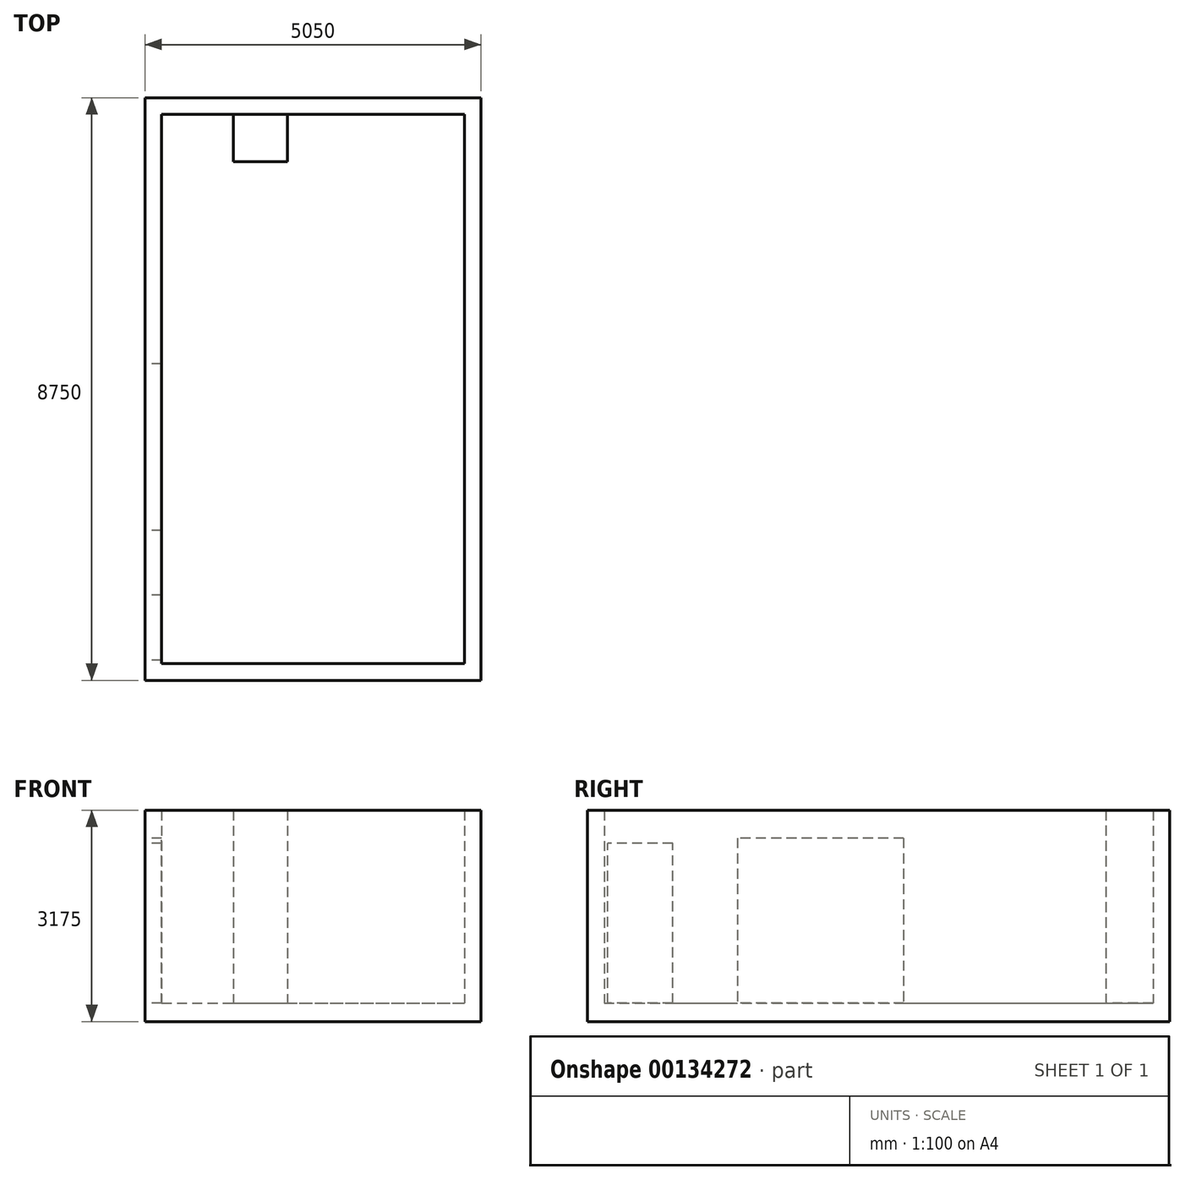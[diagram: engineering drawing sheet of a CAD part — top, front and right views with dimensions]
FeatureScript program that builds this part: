
annotation { "Feature Type Name" : "Feature", "Feature Type Description" : "" }
export const myFeature = defineFeature(function(context is Context, id is Id, definition is map)
    precondition{}
    {
        {
            var Q0;
            Q0=qCreatedBy(makeId("Top.planeOp"),FACE);
            var sketch = newSketch(context, id + "F0", { "sketchPlane" : qUnion([Q0])});
            skLineSegment(sketch, "E0.bottom", {"start": v(0, 0) * mm, "end": v(4550, 0) * mm});
            skLineSegment(sketch, "E0.top", {"start": v(0, 8250) * mm, "end": v(4550, 8250) * mm});
            skLineSegment(sketch, "E0.left", {"start": v(0, 0) * mm, "end": v(0, 8250) * mm});
            skLineSegment(sketch, "E0.right", {"start": v(4550, 0) * mm, "end": v(4550, 8250) * mm});
            skSolve(sketch);
        }
        {
            var Q0;
            Q0 = qSketchRegion(id + "F0", true);
            extrude(context, id + "F1", {"entities" : qUnion([Q0]), "depth" : 2920 * mm});
        }
        {
            var Q0;
            Q0=makeQuery(id+"F1.opExtrude","CAP_FACE",FACE,{"disambiguationData":[OSD([sQuery(id+"F0.wireOp",EDGE,"E0.bottom"),sQuery(id+"F0.wireOp",EDGE,"E0.top"),sQuery(id+"F0.wireOp",EDGE,"E0.left"),sQuery(id+"F0.wireOp",EDGE,"E0.right")])],"isStart":false});
            shell(context, id + "F2", {"entities" : qUnion([Q0]), "thickness" : 250 * mm, "oppositeDirection" : true});
        }
        {
            var Q0;
            Q0=makeQuery(id+"F2.opShell","OFFSET_FACE",FACE,{"disambiguationData":[OSD([sQuery(id+"F0.wireOp",EDGE,"E0.bottom"),sQuery(id+"F0.wireOp",EDGE,"E0.top"),sQuery(id+"F0.wireOp",EDGE,"E0.left"),sQuery(id+"F0.wireOp",EDGE,"E0.right")])]});
            extrude(context, id + "F3", {"entities" : qUnion([Q0]), "operationType" : NewBodyOperationType.ADD, "depth" : 25 * mm});
        }
        {
            var Q0;
            Q0=makeQuery(id+"F3.opExtrude","CAP_FACE",FACE,{"disambiguationData":[OSD([sQuery(id+"F0.wireOp",EDGE,"E0.bottom"),sQuery(id+"F0.wireOp",EDGE,"E0.top"),sQuery(id+"F0.wireOp",EDGE,"E0.left"),sQuery(id+"F0.wireOp",EDGE,"E0.right")])],"isStart":false});
            var sketch = newSketch(context, id + "F4", { "sketchPlane" : qUnion([Q0])});
            skLineSegment(sketch, "E1.bottom", {"start": v(1077, 8250) * mm, "end": v(1887, 8250) * mm});
            skLineSegment(sketch, "E1.top", {"start": v(1077, 7540) * mm, "end": v(1887, 7540) * mm});
            skLineSegment(sketch, "E1.left", {"start": v(1077, 8250) * mm, "end": v(1077, 7540) * mm});
            skLineSegment(sketch, "E1.right", {"start": v(1887, 8250) * mm, "end": v(1887, 7540) * mm});
            skSolve(sketch);
        }
        {
            var Q0;
            Q0 = qSketchRegion(id + "F4", true);
            extrude(context, id + "F5", {"entities" : qUnion([Q0]), "operationType" : NewBodyOperationType.ADD, "depth" : 2900 * mm});
        }
        {
            var Q0;
            Q0=makeQuery(id+"F1.opExtrude","SWEPT_FACE",FACE,{"disambiguationData":[OSD([sQuery(id+"F0.wireOp",EDGE,"E0.left")])]});
            var sketch = newSketch(context, id + "F6", { "sketchPlane" : qUnion([Q0])});
            skLineSegment(sketch, "E2.bottom", {"start": v(-1030, 25) * mm, "end": v(-50, 25) * mm});
            skLineSegment(sketch, "E2.top", {"start": v(-1030, 2425) * mm, "end": v(-50, 2425) * mm});
            skLineSegment(sketch, "E2.left", {"start": v(-1030, 25) * mm, "end": v(-1030, 2425) * mm});
            skLineSegment(sketch, "E2.right", {"start": v(-50, 25) * mm, "end": v(-50, 2425) * mm});
            skSolve(sketch);
        }
        {
            var Q0;
            Q0 = qSketchRegion(id + "F6", true);
            extrude(context, id + "F7", {"entities" : qUnion([Q0]), "operationType" : NewBodyOperationType.REMOVE, "oppositeDirection" : true, "depth" : 300 * mm});
        }
        {
            var Q0;
            Q0=makeQuery(id+"F1.opExtrude","SWEPT_FACE",FACE,{"disambiguationData":[OSD([sQuery(id+"F0.wireOp",EDGE,"E0.left")])]});
            var sketch = newSketch(context, id + "F8", { "sketchPlane" : qUnion([Q0])});
            skLineSegment(sketch, "E3.bottom", {"start": v(-4500, 2505) * mm, "end": v(-2000, 2505) * mm});
            skLineSegment(sketch, "E3.top", {"start": v(-4500, 25) * mm, "end": v(-2000, 25) * mm});
            skLineSegment(sketch, "E3.left", {"start": v(-4500, 2505) * mm, "end": v(-4500, 25) * mm});
            skLineSegment(sketch, "E3.right", {"start": v(-2000, 2505) * mm, "end": v(-2000, 25) * mm});
            skSolve(sketch);
        }
        {
            var Q0;
            Q0 = qSketchRegion(id + "F8", true);
            var Q1;
            Q1=makeQuery(id+"F2.opShell","OFFSET_FACE",FACE,{"disambiguationData":[OSD([sQuery(id+"F0.wireOp",EDGE,"E0.left")])]});
            extrude(context, id + "F9", {"entities" : qUnion([Q0]), "operationType" : NewBodyOperationType.REMOVE, "endBound" : BoundingType.UP_TO_SURFACE, "oppositeDirection" : true, "endBoundEntityFace" : qUnion([Q1]), "depth" : 25 * mm});
        }
    });
